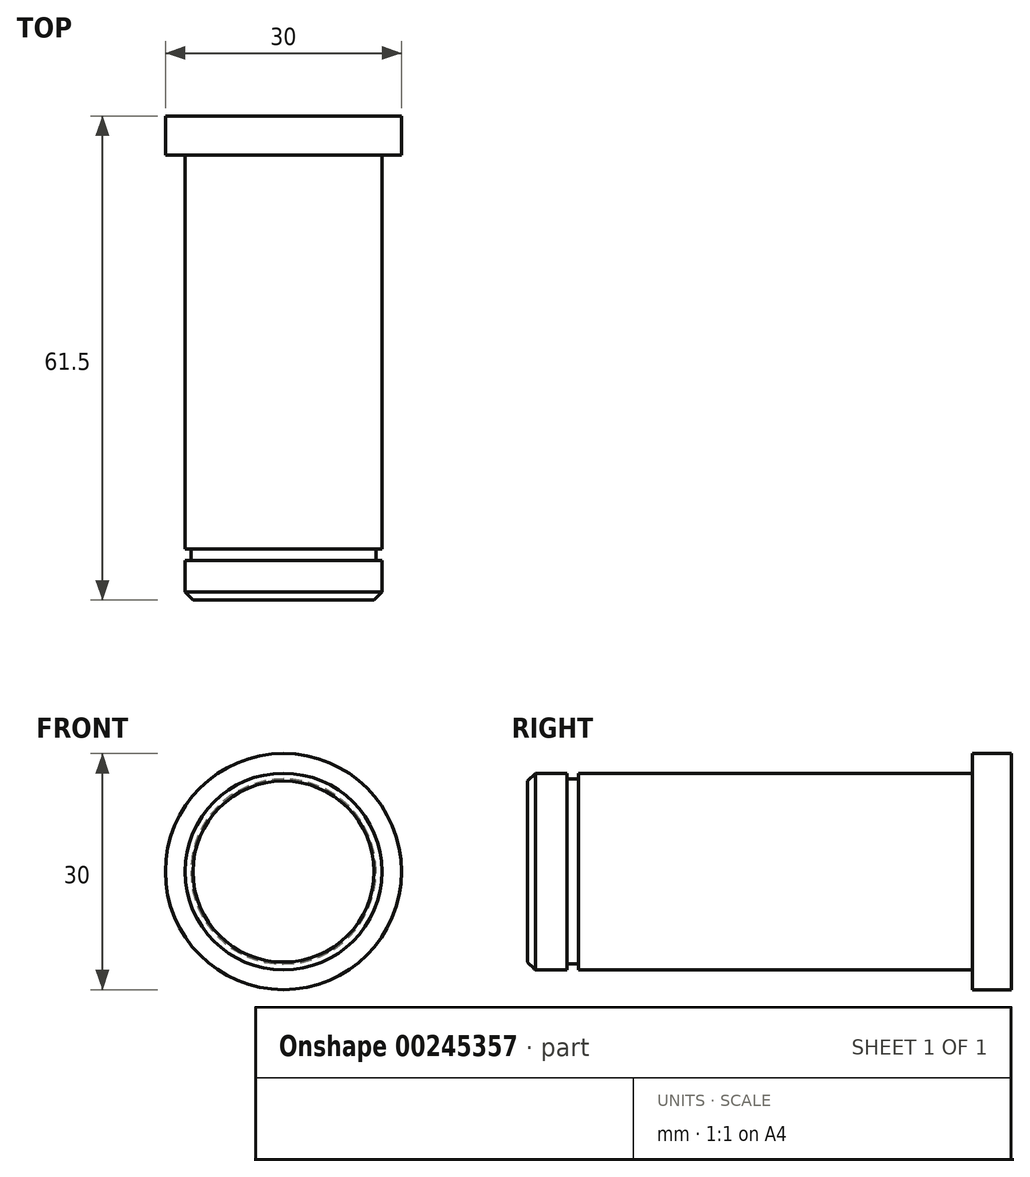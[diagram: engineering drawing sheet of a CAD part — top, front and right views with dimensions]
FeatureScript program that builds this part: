
annotation { "Feature Type Name" : "Feature", "Feature Type Description" : "" }
export const myFeature = defineFeature(function(context is Context, id is Id, definition is map)
    precondition{}
    {
        {
            var Q0;
            Q0=qCreatedBy(makeId("Front.planeOp"),FACE);
            var sketch = newSketch(context, id + "F0", { "sketchPlane" : qUnion([Q0])});
            skCircle(sketch, "E0", {"center": v(0, 0) * mm, "radius": 15 * mm});
            skSolve(sketch);
        }
        {
            var Q0;
            Q0 = qSketchRegion(id + "F0", true);
            extrude(context, id + "F1", {"entities" : qUnion([Q0]), "depth" : 5 * mm});
        }
        {
            var Q0;
            Q0=makeQuery(id+"F1.opExtrude","CAP_FACE",FACE,{"disambiguationData":[OSD([sQuery(id+"F0.wireOp",EDGE,"E0")])],"isStart":false});
            var sketch = newSketch(context, id + "F2", { "sketchPlane" : qUnion([Q0])});
            skCircle(sketch, "E1", {"center": v(0, 0) * mm, "radius": 12.5 * mm});
            skSolve(sketch);
        }
        {
            var Q0;
            Q0 = qSketchRegion(id + "F2", true);
            extrude(context, id + "F3", {"entities" : qUnion([Q0]), "operationType" : NewBodyOperationType.ADD, "depth" : 50 * mm});
        }
        {
            var Q0;
            Q0=makeQuery(id+"F3.opExtrude","CAP_FACE",FACE,{"disambiguationData":[OSD([sQuery(id+"F2.wireOp",EDGE,"E1")])],"isStart":false});
            var sketch = newSketch(context, id + "F4", { "sketchPlane" : qUnion([Q0])});
            skCircle(sketch, "E2", {"center": v(0, 0) * mm, "radius": 11.75 * mm});
            skSolve(sketch);
        }
        {
            var Q0;
            Q0 = qSketchRegion(id + "F4", true);
            extrude(context, id + "F5", {"entities" : qUnion([Q0]), "operationType" : NewBodyOperationType.ADD, "depth" : 1.5 * mm});
        }
        {
            var Q0;
            Q0=makeQuery(id+"F5.opExtrude","CAP_FACE",FACE,{"disambiguationData":[OSD([sQuery(id+"F4.wireOp",EDGE,"E2")])],"isStart":false});
            var sketch = newSketch(context, id + "F6", { "sketchPlane" : qUnion([Q0])});
            skSolve(sketch);
        }
        {
            var Q0;
            Q0=makeQuery(id+"F6.imprint","IMPRINT",FACE,{"disambiguationData":[TD([[makeQuery(id+"F6.imprint","IMPRINT",EDGE,{"derivedFrom":makeQuery(id+"F5.opExtrude","CAP_EDGE",EDGE,{"disambiguationData":[OSD([sQuery(id+"F4.wireOp",EDGE,"E2")])],"isStart":false})}),1.0]])]});
            var sketch = newSketch(context, id + "F7", { "sketchPlane" : qUnion([Q0])});
            skCircle(sketch, "E3", {"center": v(0, 0) * mm, "radius": 12.5 * mm});
            skSolve(sketch);
        }
        {
            var Q0;
            Q0 = qSketchRegion(id + "F7", true);
            extrude(context, id + "F8", {"entities" : qUnion([Q0]), "operationType" : NewBodyOperationType.ADD, "depth" : 5 * mm});
        }
        {
            var Q0;
            Q0=makeQuery(id+"F8.opExtrude","CAP_EDGE",EDGE,{"disambiguationData":[OSD([sQuery(id+"F7.wireOp",EDGE,"E3")])],"isStart":false});
            chamfer(context, id + "F9", {"entities" : qUnion([Q0]), "width" : 1 * mm, "tangentPropagation" : true});
        }
    });
